# Revit family: xShowerhead-American_Standard-Square_Rain-1660.788
name_source: partatom
category: Plumbing Fixtures
revit_build: Autodesk Revit 2014 (Build: 20130308_1515(x64)
units: mm (PartAtom-declared; Revit-internal decimal feet)

## types (1)
- 1660.788
    Assembly Code = D2010710
    CW Connection = Yes
    CWFU = 3
    Default Elevation = 0"
    Description = 8" Square Rain Showerhead
    Finish = Brass-American Standard-002-Polished Chrome
    Flow Rate = 1.8 gpm/ 9.5 L/min
    HW Connection = Yes
    HWFU = 3
    Height = 2"
    Installation Type = Wall Mounted
    Length = 7 13/16"
    Manufacturer = American Standard
    Material = Brass-American Standard-002-Polished Chrome
    Model = 1660.788
    Price = Prices may vary. Please consult Manufacturer Representative for most up-to-date price list.
    Product Documentation Link = https://www.americanstandard-us.com
    Product Page URL = https://www.americanstandard-us.com
    Specification = Showerhead shall have a Drench spray and brass ball joint. Showerhead shall have a pressure compensating control device.
    URL = https://www.americanstandard-us.com
    Vent Connection = No
    WFU = 4
    Warranty Information = One Year General Product Warranty
    Waste Connection = No
    Water Connection Diameter = 1/2"
    Water Connection Radius = 1/4"
    Width = 1"

## geometry (parser evidence)
native form markers: Sweep x2
no freeform markers — native parametric forms only
